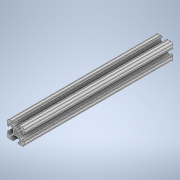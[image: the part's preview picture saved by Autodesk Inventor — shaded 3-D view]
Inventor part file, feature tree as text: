
AUTODESK INVENTOR PART (.ipt)
format: ipt  version: 2020 (Build 240168000, 168)  size: 234,496 bytes
history: native  units: in
note: dims shown in document units (in); Inventor stores cm internally (conversion verified against a paired STEP export)
features: extrude x1, sketch x1
ambient origin geometry x8: Origin, YZ Plane, XZ Plane, XY Plane, X Axis, Y Axis, Z Axis, Center Point
bodies: Solid1 (feature_tree)
feature tree (2):
  extrude  "Extrusion1"  [1 undecoded]
  sketch  "Sketch1"  dims[d0=9.0in d1=0.0in]
note: 1 required parameter value undecoded (feature->parameter linkage not recoverable at this tier; creation-order binding heuristic only, values carry confidence <= 0.55)
